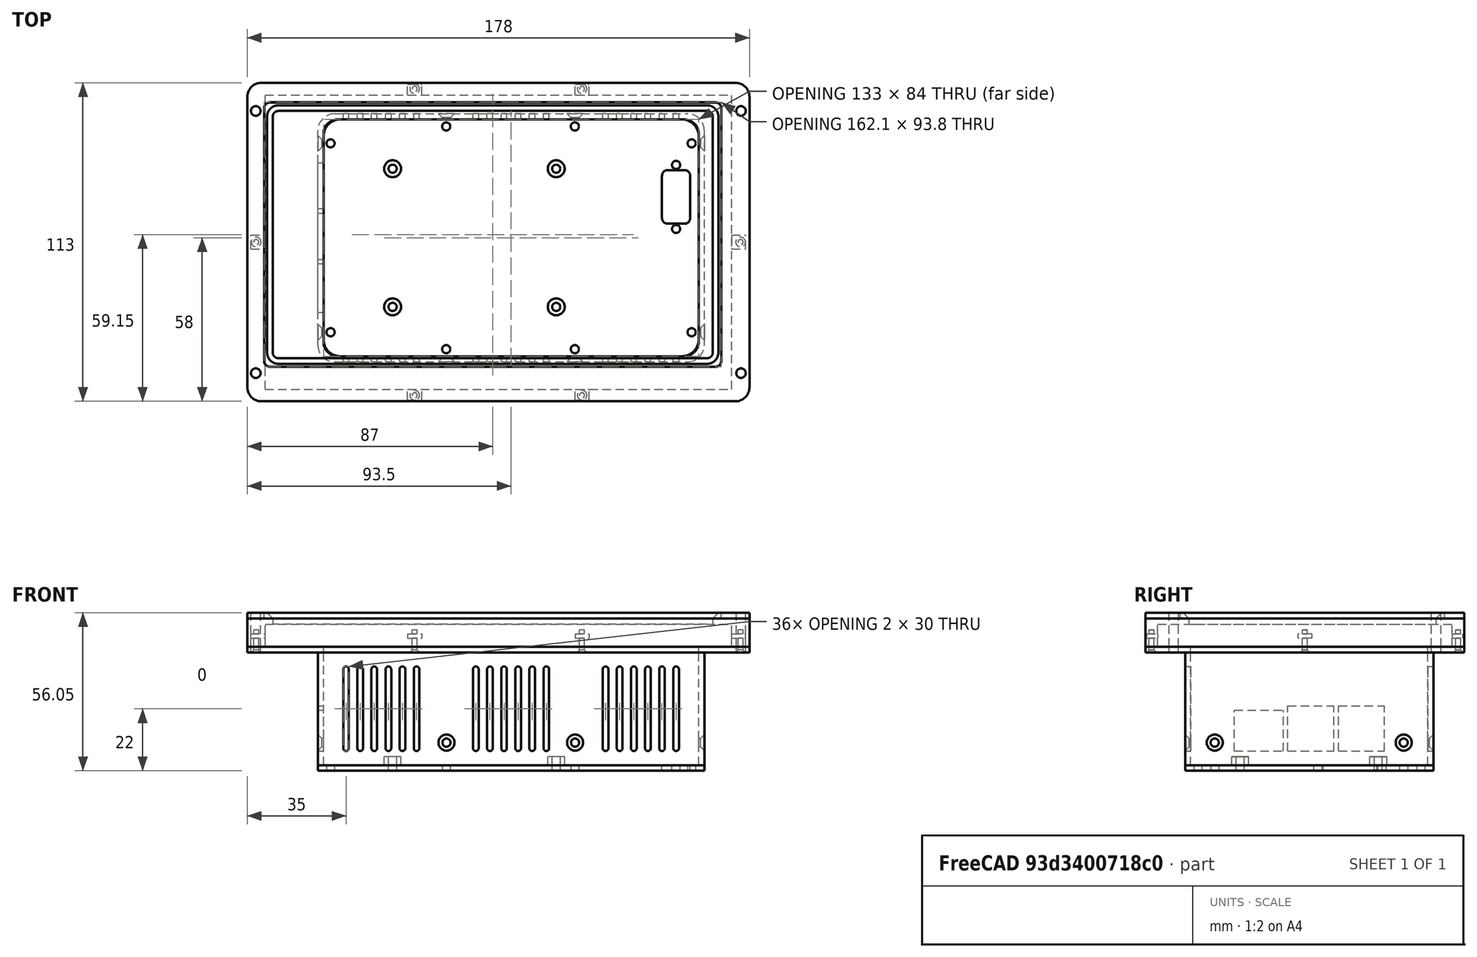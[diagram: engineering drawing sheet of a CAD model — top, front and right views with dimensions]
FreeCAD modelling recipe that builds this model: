
FCSTD DOCUMENT  (FreeCAD 0.20R29603 (Git))
Label: RPI4Soar_V2
License: All rights reserved
LicenseURL: http://en.wikipedia.org/wiki/All_rights_reserved
objects: Part::Cut×76, Part::Box×42, Part::Cylinder×28, Part::Fillet×17, Part::Fuse×5, Part::FeaturePython×4, Part::Chamfer×3, Spreadsheet::Sheet×1
note: 175 computed .brp shape members not serialized (recipe doc carries the construction recipe); baked Part::Feature solids carry a one-line shape summary decoded from their .brp

FEATURE [Spreadsheet::Sheet] Spreadsheet
  cells = A1=Display Abmessungen; C1=Toleranz; A2=Länge / mm; B2=165; C2=0.4; D2==B2 + C2; A3=Breite / mm; B3=104; C3=0.4; D3==B3 + C3; A4=Höhe / mm; B4=7.05; C4=1; D4==B4 + C4; A6=Gehäuse Dimensionen; A7=Länge / mm; B7=178; A8=Breite /mm; B8=113; A9=Höhe / mm; B9=30
FEATURE [Part::Box] Box  label="Würfel"
  AttacherType = Attacher::AttachEngine3D
  Height = 10.05
  Length = 178
  Width = 113
  expr: Height = Spreadsheet.D4 + 2
  expr: Length = Spreadsheet.B7
  expr: Width = Spreadsheet.B8
FEATURE [Part::Box] Box001  label="Würfel001"
  AttacherType = Attacher::AttachEngine3D
  Height = 8.05
  Length = 165.4
  Placement = pos=(6.3,4.3,0) rot=(0,0,1;0rad)
  Width = 104.4
  expr: .Placement.Base.x = (Spreadsheet.B7 - Spreadsheet.D2) / 2
  expr: .Placement.Base.y = (Spreadsheet.B8 - Spreadsheet.D3) / 2
  expr: Height = Spreadsheet.D4
  expr: Length = Spreadsheet.D2
  expr: Width = Spreadsheet.D3
FEATURE [Part::Cylinder] Cylinder  label="Zylinder"
  Angle = 360
  AttacherType = Attacher::AttachEngine3D
  FirstAngle = 0
  Height = 17
  Placement = pos=(3,10,-5) rot=(0,0,1;0rad)
  Radius = 1.7
  SecondAngle = 0
  expr: .Placement.Base.x = (Spreadsheet.B7 - 172) / 2
  expr: .Placement.Base.y = (Spreadsheet.B8 - 93) / 2
FEATURE [Part::Cylinder] Cylinder001  label="Zylinder001"
  Angle = 360
  AttacherType = Attacher::AttachEngine3D
  FirstAngle = 0
  Height = 17
  Placement = pos=(3,103,-5) rot=(0,0,1;0rad)
  Radius = 1.7
  SecondAngle = 0
  expr: .Placement.Base.x = (Spreadsheet.B7 - 172) / 2
  expr: .Placement.Base.y = Spreadsheet.B8 - (Spreadsheet.B8 - 93) / 2
FEATURE [Part::Cylinder] Cylinder002  label="Zylinder002"
  Angle = 360
  AttacherType = Attacher::AttachEngine3D
  FirstAngle = 0
  Height = 17
  Placement = pos=(175,10,-5) rot=(0,0,1;0rad)
  Radius = 1.7
  SecondAngle = 0
  expr: .Placement.Base.x = Spreadsheet.B7 - (Spreadsheet.B7 - 172) / 2
  expr: .Placement.Base.y = (Spreadsheet.B8 - 93) / 2
FEATURE [Part::Cylinder] Cylinder003  label="Zylinder003"
  Angle = 360
  AttacherType = Attacher::AttachEngine3D
  FirstAngle = 0
  Height = 17
  Placement = pos=(175,103,-5) rot=(0,0,1;0rad)
  Radius = 1.7
  SecondAngle = 0
  expr: .Placement.Base.x = Spreadsheet.B7 - (Spreadsheet.B7 - 172) / 2
  expr: .Placement.Base.y = Spreadsheet.B8 - (Spreadsheet.B8 - 93) / 2
FEATURE [Part::Box] Box004  label="Würfel004"
  AttacherType = Attacher::AttachEngine3D
  Height = 2
  Length = 178
  Placement = pos=(0,0,-2) rot=(0,0,1;0rad)
  Width = 113
  expr: Length = Spreadsheet.B7
  expr: Width = Spreadsheet.B8
FEATURE [Part::Box] Box005  label="Würfel005"
  AttacherType = Attacher::AttachEngine3D
  Height = 15
  Length = 133
  Placement = pos=(27,16,-14) rot=(0,0,1;0rad)
  Width = 84
FEATURE [Part::Box] Box006  label="Würfel006"
  AttacherType = Attacher::AttachEngine3D
  Height = 7.05
  Length = 156
  Placement = pos=(9,15.3,3) rot=(0,0,1;0rad)
  Width = 87.7
  expr: .Placement.Base.x = 15.5 - 6.5
  expr: .Placement.Base.y = 20.8 - 5.5
  expr: Height = Spreadsheet.B4
FEATURE [Part::Fillet] Fillet003
  Base = -> Box005
  Edges = 4 edges r=5: [Edge1,Edge3,Edge5,Edge7]
FEATURE [Part::Cut] Cut011
  Base = -> Box004
  Tool = -> Fillet003
FEATURE [Part::Cut] Cut012
  Base = -> Cut011
  Tool = -> Cylinder001
FEATURE [Part::Cut] Cut013
  Base = -> Cut012
  Tool = -> Cylinder002
FEATURE [Part::Cut] Cut014
  Base = -> Cut013
  Tool = -> Cylinder003
FEATURE [Part::Cut] Cut015
  Base = -> Cut014
  Tool = -> Cylinder
FEATURE [Part::Fillet] Fillet004
  Base = -> Cut015
  Edges = 4 edges r=5: [Edge1,Edge3,Edge6,Edge23]
FEATURE [Part::Box] Box007  label="Würfel007"
  AttacherType = Attacher::AttachEngine3D
  Height = 40
  Length = 133
  Placement = pos=(27,16,-42) rot=(0,0,1;0rad)
  Width = 84
FEATURE [Part::Box] Box008  label="Würfel008"
  AttacherType = Attacher::AttachEngine3D
  Height = 40
  Length = 137
  Placement = pos=(25,14,-42) rot=(0,0,1;0rad)
  Width = 88
FEATURE [Part::Box] Box010  label="Würfel010"
  AttacherType = Attacher::AttachEngine3D
  Height = 2
  Length = 137
  Placement = pos=(25,14,-44) rot=(0,0,1;0rad)
  Width = 88
FEATURE [Part::Cylinder] Cylinder008  label="Zylinder008"
  Angle = 360
  AttacherType = Attacher::AttachEngine3D
  FirstAngle = 0
  Height = 108
  Placement = pos=(116.2,114,-34) rot=(1,0,0;1.5708rad)
  Radius = 1.45
  SecondAngle = 0
FEATURE [Part::Cylinder] Cylinder010  label="Zylinder010"
  Angle = 360
  AttacherType = Attacher::AttachEngine3D
  FirstAngle = 0
  Height = 155
  Placement = pos=(14,24.5,-34) rot=(0,1,0;1.5708rad)
  Radius = 1.45
  SecondAngle = 0
FEATURE [Part::Cylinder] Cylinder011  label="Zylinder011"
  Angle = 360
  AttacherType = Attacher::AttachEngine3D
  FirstAngle = 0
  Height = 157
  Placement = pos=(14,91.5,-34) rot=(0,1,0;1.5708rad)
  Radius = 1.45
  SecondAngle = 0
FEATURE [Part::Cylinder] Cylinder012  label="Zylinder012"
  Angle = 360
  AttacherType = Attacher::AttachEngine3D
  FirstAngle = 0
  Height = 10
  Placement = pos=(109.5,33.5,-49) rot=(0,0,1;0rad)
  Radius = 1.45
  SecondAngle = 0
  expr: .Placement.Base.y = 35 - 1.5
FEATURE [Part::Cylinder] Cylinder013  label="Zylinder013"
  Angle = 360
  AttacherType = Attacher::AttachEngine3D
  FirstAngle = 0
  Height = 10
  Placement = pos=(51.5,82.5,-49) rot=(0,0,1;0rad)
  Radius = 1.45
  SecondAngle = 0
  expr: .Placement.Base.y = 35 + 49 - 1.5
FEATURE [Part::Cylinder] Cylinder014  label="Zylinder014"
  Angle = 360
  AttacherType = Attacher::AttachEngine3D
  FirstAngle = 0
  Height = 10
  Placement = pos=(51.5,33.5,-49) rot=(0,0,1;0rad)
  Radius = 1.45
  SecondAngle = 0
  expr: .Placement.Base.y = 35 - 1.5
FEATURE [Part::Cylinder] Cylinder015  label="Zylinder015"
  Angle = 360
  AttacherType = Attacher::AttachEngine3D
  FirstAngle = 0
  Height = 10
  Placement = pos=(109.5,82.5,-49) rot=(0,0,1;0rad)
  Radius = 1.45
  SecondAngle = 0
  expr: .Placement.Base.y = 35 + 49 - 1.5
FEATURE [Part::Box] Box017  label="Würfel017"
  AttacherType = Attacher::AttachEngine3D
  Height = 10
  Length = 10
  Placement = pos=(147,63,-49) rot=(0,0,1;0rad)
  Width = 19
FEATURE [Part::Cylinder] Cylinder020  label="Zylinder020"
  Angle = 360
  AttacherType = Attacher::AttachEngine3D
  FirstAngle = 0
  Height = 10
  Placement = pos=(152,83.85,-49) rot=(0,0,1;0rad)
  Radius = 1.45
  SecondAngle = 0
FEATURE [Part::Cylinder] Cylinder021  label="Zylinder021"
  Angle = 360
  AttacherType = Attacher::AttachEngine3D
  FirstAngle = 0
  Height = 10
  Placement = pos=(152,61.15,-49) rot=(0,0,1;0rad)
  Radius = 1.45
  SecondAngle = 0
FEATURE [Part::Cylinder] Cylinder022  label="Zylinder022"
  Angle = 360
  AttacherType = Attacher::AttachEngine3D
  FirstAngle = 0
  Height = 10
  Placement = pos=(59.3333,2.15,-4) rot=(0,0,1;0rad)
  Radius = 0.9
  SecondAngle = 0
  expr: .Placement.Base.x = Spreadsheet.B7 / 3
  expr: .Placement.Base.y = (Spreadsheet.B8 - Spreadsheet.D3) / 4
FEATURE [Part::Cylinder] Cylinder023  label="Zylinder023"
  Angle = 360
  AttacherType = Attacher::AttachEngine3D
  FirstAngle = 0
  Height = 10
  Placement = pos=(118.667,2.15,-4) rot=(0,0,1;0rad)
  Radius = 0.9
  SecondAngle = 0
  expr: .Placement.Base.x = Spreadsheet.B7 / 3 * 2
  expr: .Placement.Base.y = (Spreadsheet.B8 - Spreadsheet.D3) / 4
FEATURE [Part::Box] Box018  label="Würfel018"
  AttacherType = Attacher::AttachEngine3D
  Height = 1.5
  Length = 5
  Placement = pos=(56.8333,0.5,3) rot=(0,0,1;0rad)
  Width = 4
  expr: .Placement.Base.x = Spreadsheet.B7 / 3 - 2.5
FEATURE [Part::Box] Box019  label="Würfel019"
  AttacherType = Attacher::AttachEngine3D
  Height = 1.5
  Length = 5
  Placement = pos=(116.167,0.5,3) rot=(0,0,1;0rad)
  Width = 4
  expr: .Placement.Base.x = Spreadsheet.B7 / 3 * 2 - 2.5
FEATURE [Part::Cylinder] Cylinder024  label="Zylinder024"
  Angle = 360
  AttacherType = Attacher::AttachEngine3D
  FirstAngle = 0
  Height = 10
  Placement = pos=(59.3333,110.85,-4) rot=(0,0,1;0rad)
  Radius = 0.9
  SecondAngle = 0
  expr: .Placement.Base.x = Spreadsheet.B7 / 3
  expr: .Placement.Base.y = Spreadsheet.B8 - (Spreadsheet.B8 - Spreadsheet.D3) / 4
FEATURE [Part::Cylinder] Cylinder025  label="Zylinder025"
  Angle = 360
  AttacherType = Attacher::AttachEngine3D
  FirstAngle = 0
  Height = 10
  Placement = pos=(118.667,110.85,-4) rot=(0,0,1;0rad)
  Radius = 0.9
  SecondAngle = 0
  expr: .Placement.Base.x = Spreadsheet.B7 / 3 * 2
  expr: .Placement.Base.y = Spreadsheet.B8 - (Spreadsheet.B8 - Spreadsheet.D3) / 4
FEATURE [Part::Box] Box020  label="Würfel020"
  AttacherType = Attacher::AttachEngine3D
  Height = 1.5
  Length = 5
  Placement = pos=(56.8333,108.5,3) rot=(0,0,1;0rad)
  Width = 4
  expr: .Placement.Base.x = Spreadsheet.B7 / 3 - 2.5
FEATURE [Part::Cylinder] Cylinder026  label="Zylinder026"
  Angle = 360
  AttacherType = Attacher::AttachEngine3D
  FirstAngle = 0
  Height = 10
  Placement = pos=(3.15,56.5,-4) rot=(0,0,1;0rad)
  Radius = 0.9
  SecondAngle = 0
  expr: .Placement.Base.x = (Spreadsheet.B7 - Spreadsheet.D2) / 4
  expr: .Placement.Base.y = Spreadsheet.B8 / 2
FEATURE [Part::Cylinder] Cylinder027  label="Zylinder027"
  Angle = 360
  AttacherType = Attacher::AttachEngine3D
  FirstAngle = 0
  Height = 10
  Placement = pos=(174.85,56.5,-4) rot=(0,0,1;0rad)
  Radius = 0.9
  SecondAngle = 0
  expr: .Placement.Base.x = Spreadsheet.B7 - (Spreadsheet.B7 - Spreadsheet.D2) / 4
  expr: .Placement.Base.y = Spreadsheet.B8 / 2
FEATURE [Part::Box] Box021  label="Würfel021"
  AttacherType = Attacher::AttachEngine3D
  Height = 1.5
  Length = 6
  Placement = pos=(1.3,54,3) rot=(0,0,1;0rad)
  Width = 5
  expr: .Placement.Base.y = Spreadsheet.B8 / 2 - 2.5
FEATURE [Part::Box] Box022  label="Würfel022"
  AttacherType = Attacher::AttachEngine3D
  Height = 1.5
  Length = 6
  Placement = pos=(170.7,54,3) rot=(0,0,1;0rad)
  Width = 5
  expr: .Placement.Base.y = Spreadsheet.B8 / 2 - 2.5
FEATURE [Part::Cut] Cut
  Base = -> Box
  Tool = -> Box001
FEATURE [Part::Cut] Cut038
  Base = -> Cut
  Tool = -> Box006
FEATURE [Part::Fillet] Fillet
  Base = -> Cut038
  Edges = 4 edges r=5: [Edge1,Edge3,Edge6,Edge15]
FEATURE [Part::Cut] Cut054
  Base = -> Box008
  Tool = -> Box007
FEATURE [Part::Cut] Cut060
  Base = -> Fillet004
  Tool = -> Cylinder022
FEATURE [Part::Cut] Cut061
  Base = -> Cut060
  Tool = -> Cylinder022
FEATURE [Part::Cut] Cut062
  Base = -> Cut061
  Tool = -> Cylinder024
FEATURE [Part::Cut] Cut063
  Base = -> Cut062
  Tool = -> Cylinder025
FEATURE [Part::Cut] Cut064
  Base = -> Cut063
  Tool = -> Cylinder026
FEATURE [Part::Cut] Cut065
  Base = -> Cut064
  Tool = -> Cylinder027
FEATURE [Part::Cut] Cut066
  Base = -> Cut065
  Tool = -> Cylinder023
FEATURE [Part::Box] Box023  label="Würfel023"
  AttacherType = Attacher::AttachEngine3D
  Height = 1.5
  Length = 5
  Placement = pos=(116.167,108.5,3) rot=(0,0,1;0rad)
  Width = 4
  expr: .Placement.Base.x = Spreadsheet.B7 / 3 * 2 - 2.5
FEATURE [Part::Cylinder] Cylinder032  label="Zylinder032"
  Angle = 360
  AttacherType = Attacher::AttachEngine3D
  FirstAngle = 0
  Height = 108
  Placement = pos=(70.6,114,-34) rot=(1,0,0;1.5708rad)
  Radius = 1.45
  SecondAngle = 0
FEATURE [Part::Cylinder] Cylinder033  label="Zylinder033"
  Angle = 360
  AttacherType = Attacher::AttachEngine3D
  FirstAngle = 0
  Height = 10
  Placement = pos=(116.1,97.5,-49) rot=(0,0,1;0rad)
  Radius = 1.45
  SecondAngle = 0
FEATURE [Part::Cylinder] Cylinder034  label="Zylinder034"
  Angle = 360
  AttacherType = Attacher::AttachEngine3D
  FirstAngle = 0
  Height = 10
  Placement = pos=(116.1,18.5,-49) rot=(0,0,1;0rad)
  Radius = 1.45
  SecondAngle = 0
FEATURE [Part::Cylinder] Cylinder035  label="Zylinder035"
  Angle = 360
  AttacherType = Attacher::AttachEngine3D
  FirstAngle = 0
  Height = 10
  Placement = pos=(70.5,97.5,-49) rot=(0,0,1;0rad)
  Radius = 1.45
  SecondAngle = 0
FEATURE [Part::Cylinder] Cylinder036  label="Zylinder036"
  Angle = 360
  AttacherType = Attacher::AttachEngine3D
  FirstAngle = 0
  Height = 10
  Placement = pos=(70.5,18.5,-49) rot=(0,0,1;0rad)
  Radius = 1.45
  SecondAngle = 0
FEATURE [Part::Cylinder] Cylinder037  label="Zylinder037"
  Angle = 360
  AttacherType = Attacher::AttachEngine3D
  FirstAngle = 0
  Height = 10
  Placement = pos=(29.5,91.5,-49) rot=(0,0,1;0rad)
  Radius = 1.45
  SecondAngle = 0
FEATURE [Part::Cylinder] Cylinder038  label="Zylinder038"
  Angle = 360
  AttacherType = Attacher::AttachEngine3D
  FirstAngle = 0
  Height = 10
  Placement = pos=(157.5,91.5,-49) rot=(0,0,1;0rad)
  Radius = 1.45
  SecondAngle = 0
FEATURE [Part::Cylinder] Cylinder039  label="Zylinder039"
  Angle = 360
  AttacherType = Attacher::AttachEngine3D
  FirstAngle = 0
  Height = 10
  Placement = pos=(157.5,24.5,-49) rot=(0,0,1;0rad)
  Radius = 1.45
  SecondAngle = 0
FEATURE [Part::Cylinder] Cylinder040  label="Zylinder040"
  Angle = 360
  AttacherType = Attacher::AttachEngine3D
  FirstAngle = 0
  Height = 10
  Placement = pos=(29.5,24.5,-49) rot=(0,0,1;0rad)
  Radius = 1.45
  SecondAngle = 0
FEATURE [Part::Cut] Cut089
  Base = -> Cut054
  Tool = -> Cylinder008
FEATURE [Part::Cut] Cut090
  Base = -> Cut089
  Tool = -> Cylinder010
FEATURE [Part::Cut] Cut091
  Base = -> Cut090
  Tool = -> Cylinder011
FEATURE [Part::Cut] Cut092
  Base = -> Cut091
  Tool = -> Cylinder032
FEATURE [Part::Fillet] Fillet013
  Base = -> Cut092
  Edges = 8 edges r=6: [Edge1,Edge4,Edge8,Edge24,Edge37,Edge38,Edge39,Edge40]
FEATURE [Part::Fillet] Fillet014
  Base = -> Box010
  Edges = 4 edges r=6: [Edge1,Edge3,Edge5,Edge7]
FEATURE [Part::Cut] Cut093
  Base = -> Fillet014
  Tool = -> Cylinder033
FEATURE [Part::Cut] Cut094
  Base = -> Cut093
  Tool = -> Cylinder034
FEATURE [Part::Cut] Cut095
  Base = -> Cut094
  Tool = -> Cylinder035
FEATURE [Part::Cut] Cut096
  Base = -> Cut095
  Tool = -> Cylinder036
FEATURE [Part::Cut] Cut097
  Base = -> Cut096
  Tool = -> Cylinder037
FEATURE [Part::Cut] Cut098
  Base = -> Cut097
  Tool = -> Cylinder038
FEATURE [Part::Cut] Cut099
  Base = -> Cut098
  Tool = -> Cylinder039
FEATURE [Part::Cut] Cut100
  Base = -> Cut099
  Tool = -> Cylinder040
FEATURE [Part::Cut] Cut101
  Base = -> Cut100
  Tool = -> Cylinder012
FEATURE [Part::Cut] Cut102
  Base = -> Cut101
  Tool = -> Cylinder013
FEATURE [Part::Cut] Cut103
  Base = -> Cut102
  Tool = -> Cylinder014
FEATURE [Part::Cut] Cut104
  Base = -> Cut103
  Tool = -> Cylinder015
FEATURE [Part::FeaturePython] Tube  label="Spacer"  # WARN: FeaturePython — macro-defined, semantics opaque (R4)
  AttacherType = Attacher::AttachEngine3D
  Height = 3
  InnerRadius = 1.45
  OuterRadius = 3
  Placement = pos=(109.5,33.5,-42) rot=(0,0,1;0rad)
FEATURE [Part::Chamfer] Chamfer005
  Base = -> Fillet013
  Edges = 8 edges r=1.4: [Edge5,Edge6,Edge44,Edge45,Edge47,Edge48,Edge51,Edge52]
FEATURE [Part::Fuse] Fusion021
  Base = -> Chamfer005
  Tool = -> Cut066
FEATURE [Part::Chamfer] Chamfer006
  Base = -> Fusion021
  Edges = 6 edges r=0.8: [Edge18,Edge19,Edge21,Edge23,Edge31,Edge32]
FEATURE [Part::Box] Box034  label="Würfel034"
  AttacherType = Attacher::AttachEngine3D
  Height = 14.5
  Length = 2
  Placement = pos=(25,31.5,-37) rot=(0,0,1;0rad)
  Width = 17.3
FEATURE [Part::Box] Box035  label="Würfel035"
  AttacherType = Attacher::AttachEngine3D
  Height = 16
  Length = 2
  Placement = pos=(25,50.4,-37) rot=(0,0,1;0rad)
  Width = 16.3
FEATURE [Part::Box] Box036  label="Würfel036"
  AttacherType = Attacher::AttachEngine3D
  Height = 16
  Length = 2
  Placement = pos=(25,68.4,-37) rot=(0,0,1;0rad)
  Width = 16.3
FEATURE [Part::Cut] Cut105
  Base = -> Chamfer006
  Tool = -> Box034
FEATURE [Part::Cut] Cut106
  Base = -> Cut105
  Tool = -> Box035
FEATURE [Part::Cut] Cut107  label="Housing_1"
  Base = -> Cut106
  Tool = -> Box036
FEATURE [Part::Fillet] Fillet015
  Base = -> Box017
  Edges = 4 edges r=2: [Edge1,Edge3,Edge5,Edge7]
FEATURE [Part::Cut] Cut108
  Base = -> Cut104
  Tool = -> Fillet015
FEATURE [Part::Cut] Cut109
  Base = -> Cut108
  Tool = -> Cylinder020
FEATURE [Part::Cut] Cut110  label="Backplate"
  Base = -> Cut109
  Tool = -> Cylinder021
FEATURE [Part::FeaturePython] Tube001  label="Spacer1"  # WARN: FeaturePython — macro-defined, semantics opaque (R4)
  AttacherType = Attacher::AttachEngine3D
  Height = 3
  InnerRadius = 1.45
  OuterRadius = 3
  Placement = pos=(51.5,33.5,-42) rot=(0,0,1;0rad)
FEATURE [Part::FeaturePython] Tube002  label="Spacer2"  # WARN: FeaturePython — macro-defined, semantics opaque (R4)
  AttacherType = Attacher::AttachEngine3D
  Height = 3
  InnerRadius = 1.45
  OuterRadius = 3
  Placement = pos=(109.5,82.5,-42) rot=(0,0,1;0rad)
FEATURE [Part::FeaturePython] Tube003  label="Spacer3"  # WARN: FeaturePython — macro-defined, semantics opaque (R4)
  AttacherType = Attacher::AttachEngine3D
  Height = 3
  InnerRadius = 1.45
  OuterRadius = 3
  Placement = pos=(51.5,82.5,-42) rot=(0,0,1;0rad)
FEATURE [Part::Box] Box037  label="Würfel037"
  AttacherType = Attacher::AttachEngine3D
  Height = 30
  Length = 2
  Placement = pos=(34,0,-37) rot=(0,0,1;0rad)
  Width = 113
FEATURE [Part::Box] Box038  label="Würfel038"
  AttacherType = Attacher::AttachEngine3D
  Height = 30
  Length = 2
  Placement = pos=(39,0,-37) rot=(0,0,1;0rad)
  Width = 113
FEATURE [Part::Box] Box039  label="Würfel039"
  AttacherType = Attacher::AttachEngine3D
  Height = 30
  Length = 2
  Placement = pos=(44,0,-37) rot=(0,0,1;0rad)
  Width = 113
FEATURE [Part::Box] Box040  label="Würfel040"
  AttacherType = Attacher::AttachEngine3D
  Height = 30
  Length = 2
  Placement = pos=(49,0,-37) rot=(0,0,1;0rad)
  Width = 113
FEATURE [Part::Box] Box041  label="Würfel041"
  AttacherType = Attacher::AttachEngine3D
  Height = 30
  Length = 2
  Placement = pos=(54,0,-37) rot=(0,0,1;0rad)
  Width = 113
FEATURE [Part::Box] Box042  label="Würfel042"
  AttacherType = Attacher::AttachEngine3D
  Height = 30
  Length = 2
  Placement = pos=(59,0,-37) rot=(0,0,1;0rad)
  Width = 113
FEATURE [Part::Box] Box043  label="Würfel043"
  AttacherType = Attacher::AttachEngine3D
  Height = 30
  Length = 2
  Placement = pos=(80,0,-37) rot=(0,0,1;0rad)
  Width = 113
FEATURE [Part::Box] Box044  label="Würfel044"
  AttacherType = Attacher::AttachEngine3D
  Height = 30
  Length = 2
  Placement = pos=(85,0,-37) rot=(0,0,1;0rad)
  Width = 113
FEATURE [Part::Box] Box045  label="Würfel045"
  AttacherType = Attacher::AttachEngine3D
  Height = 30
  Length = 2
  Placement = pos=(90,0,-37) rot=(0,0,1;0rad)
  Width = 113
FEATURE [Part::Box] Box046  label="Würfel046"
  AttacherType = Attacher::AttachEngine3D
  Height = 30
  Length = 2
  Placement = pos=(95,0,-37) rot=(0,0,1;0rad)
  Width = 113
FEATURE [Part::Box] Box047  label="Würfel047"
  AttacherType = Attacher::AttachEngine3D
  Height = 30
  Length = 2
  Placement = pos=(100,0,-37) rot=(0,0,1;0rad)
  Width = 113
FEATURE [Part::Box] Box048  label="Würfel048"
  AttacherType = Attacher::AttachEngine3D
  Height = 30
  Length = 2
  Placement = pos=(105,0,-37) rot=(0,0,1;0rad)
  Width = 113
FEATURE [Part::Box] Box049  label="Würfel049"
  AttacherType = Attacher::AttachEngine3D
  Height = 30
  Length = 2
  Placement = pos=(126,0,-37) rot=(0,0,1;0rad)
  Width = 113
FEATURE [Part::Box] Box050  label="Würfel050"
  AttacherType = Attacher::AttachEngine3D
  Height = 30
  Length = 2
  Placement = pos=(131,0,-37) rot=(0,0,1;0rad)
  Width = 113
FEATURE [Part::Box] Box051  label="Würfel051"
  AttacherType = Attacher::AttachEngine3D
  Height = 30
  Length = 2
  Placement = pos=(136,0,-37) rot=(0,0,1;0rad)
  Width = 113
FEATURE [Part::Box] Box052  label="Würfel052"
  AttacherType = Attacher::AttachEngine3D
  Height = 30
  Length = 2
  Placement = pos=(141,0,-37) rot=(0,0,1;0rad)
  Width = 113
FEATURE [Part::Box] Box053  label="Würfel053"
  AttacherType = Attacher::AttachEngine3D
  Height = 30
  Length = 2
  Placement = pos=(146,0,-37) rot=(0,0,1;0rad)
  Width = 113
FEATURE [Part::Box] Box054  label="Würfel054"
  AttacherType = Attacher::AttachEngine3D
  Height = 30
  Length = 2
  Placement = pos=(151,0,-37) rot=(0,0,1;0rad)
  Width = 113
FEATURE [Part::Cut] Cut111
  Base = -> Cut107
  Tool = -> Box037
FEATURE [Part::Cut] Cut112
  Base = -> Cut111
  Tool = -> Box038
FEATURE [Part::Cut] Cut113
  Base = -> Cut112
  Tool = -> Box039
FEATURE [Part::Cut] Cut114
  Base = -> Cut113
  Tool = -> Box040
FEATURE [Part::Cut] Cut115
  Base = -> Cut114
  Tool = -> Box041
FEATURE [Part::Cut] Cut116
  Base = -> Cut115
  Tool = -> Box042
FEATURE [Part::Cut] Cut117
  Base = -> Cut116
  Tool = -> Box043
FEATURE [Part::Cut] Cut118
  Base = -> Cut117
  Tool = -> Box044
FEATURE [Part::Cut] Cut119
  Base = -> Cut118
  Tool = -> Box045
FEATURE [Part::Cut] Cut120
  Base = -> Cut119
  Tool = -> Box046
FEATURE [Part::Cut] Cut121
  Base = -> Cut120
  Tool = -> Box047
FEATURE [Part::Cut] Cut122
  Base = -> Cut121
  Tool = -> Box048
FEATURE [Part::Cut] Cut123
  Base = -> Cut122
  Tool = -> Box049
FEATURE [Part::Cut] Cut124
  Base = -> Cut123
  Tool = -> Box050
FEATURE [Part::Cut] Cut125
  Base = -> Cut124
  Tool = -> Box051
FEATURE [Part::Cut] Cut126
  Base = -> Cut125
  Tool = -> Box052
FEATURE [Part::Cut] Cut127
  Base = -> Cut126
  Tool = -> Box053
FEATURE [Part::Cut] Cut128  label="housing2"
  Base = -> Cut127
  Tool = -> Box054
FEATURE [Part::Box] Box055  label="Würfel055"
  AttacherType = Attacher::AttachEngine3D
  Height = 2
  Length = 162
  Placement = pos=(6,12.3,10.05) rot=(0,0,1;0rad)
  Width = 3
FEATURE [Part::Box] Box056  label="Würfel056"
  AttacherType = Attacher::AttachEngine3D
  Height = 2
  Length = 162
  Placement = pos=(6,103,10.05) rot=(0,0,1;0rad)
  Width = 3
FEATURE [Part::Box] Box057  label="Würfel057"
  AttacherType = Attacher::AttachEngine3D
  Height = 2
  Length = 3
  Placement = pos=(6,12.3,10.05) rot=(0,0,1;0rad)
  Width = 93.7
FEATURE [Part::Box] Box058  label="Würfel058"
  AttacherType = Attacher::AttachEngine3D
  Height = 2
  Length = 3
  Placement = pos=(165,12.3,10.05) rot=(0,0,1;0rad)
  Width = 93.7
FEATURE [Part::Cut] Cut129
  Base = -> Fillet
  Tool = -> Box018
FEATURE [Part::Cut] Cut130
  Base = -> Cut129
  Tool = -> Box019
FEATURE [Part::Cut] Cut131
  Base = -> Cut130
  Tool = -> Box020
FEATURE [Part::Cut] Cut132
  Base = -> Cut131
  Tool = -> Box021
FEATURE [Part::Cut] Cut133
  Base = -> Cut132
  Tool = -> Box022
FEATURE [Part::Cut] Cut134
  Base = -> Cut133
  Tool = -> Box023
FEATURE [Part::Cut] Cut135
  Base = -> Cut134
  Tool = -> Cylinder023
FEATURE [Part::Cut] Cut136
  Base = -> Cut135
  Tool = -> Cylinder024
FEATURE [Part::Cut] Cut137
  Base = -> Cut136
  Tool = -> Cylinder025
FEATURE [Part::Cut] Cut138
  Base = -> Cut137
  Tool = -> Cylinder026
FEATURE [Part::Cut] Cut139
  Base = -> Cut138
  Tool = -> Cylinder027
FEATURE [Part::Cut] Cut140
  Base = -> Cut139
  Tool = -> Cylinder022
FEATURE [Part::Cut] Cut141
  Base = -> Cut140
  Tool = -> Cylinder
FEATURE [Part::Cut] Cut142
  Base = -> Cut141
  Tool = -> Cylinder001
FEATURE [Part::Cut] Cut143
  Base = -> Cut142
  Tool = -> Cylinder002
FEATURE [Part::Cut] Cut144
  Base = -> Cut143
  Tool = -> Cylinder003
FEATURE [Part::Fillet] Fillet017
  Base = -> Cut128
  Edges = 24 edges r=0.99: [Edge296,Edge297,Edge299,Edge301,Edge304,Edge305,Edge307,Edge309,Edge312,Edge313,Edge315,Edge317,Edge320,Edge321,Edge323,Edge325,Edge328,Edge329,Edge331,Edge333,Edge336,Edge337,Edge339,Edge341]
FEATURE [Part::Fillet] Fillet018
  Base = -> Fillet017
  Edges = 23 edges r=0.99: [Edge163,Edge164,Edge166,Edge168,Edge171,Edge172,Edge174,Edge176,Edge179,Edge180,Edge182,Edge184,Edge189,Edge190,Edge192,Edge194,Edge197,Edge198,Edge200,Edge202,Edge206,Edge208,Edge210]
FEATURE [Part::Fillet] Fillet019
  Base = -> Fillet018
  Edges = 1 edges r=0.99: [Edge396]
FEATURE [Part::Fillet] Fillet020
  Base = -> Fillet019
  Edges = 24 edges r=0.99: [Edge221,Edge222,Edge224,Edge226,Edge229,Edge230,Edge232,Edge234,Edge237,Edge238,Edge240,Edge242,Edge245,Edge246,Edge248,Edge250,Edge253,Edge254,Edge256,Edge258,Edge261,Edge262,Edge264,Edge266]
FEATURE [Part::Fillet] Fillet021
  Base = -> Fillet020
  Edges = 23 edges r=0.99: [Edge798,Edge799,Edge801,Edge802,Edge803,Edge804,Edge805,Edge806,Edge807,Edge808,Edge809,Edge810,Edge811,Edge812,Edge813,Edge814,Edge815,Edge816,Edge817,Edge818,Edge819,Edge820,Edge821]
FEATURE [Part::Fillet] Fillet022
  Base = -> Fillet021
  Edges = 1 edges r=0.99: [Edge110]
FEATURE [Part::Fillet] Fillet023
  Base = -> Fillet022
  Edges = 24 edges r=0.99: [Edge211,Edge213,Edge215,Edge217,Edge219,Edge221,Edge223,Edge225,Edge227,Edge229,Edge231,Edge233,Edge237,Edge239,Edge241,Edge243,Edge245,Edge247,Edge249,Edge251,Edge253,Edge255,Edge257,Edge259]
FEATURE [Part::Fillet] Fillet024  label="housing"
  Base = -> Fillet023
  Edges = 24 edges r=0.99: [Edge203,Edge205,Edge207,Edge209,Edge211,Edge213,Edge215,Edge217,Edge219,Edge221,Edge223,Edge225,Edge227,Edge229,Edge231,Edge233,Edge235,Edge237,Edge239,Edge241,Edge243,Edge245,Edge247,Edge249]
FEATURE [Part::Fuse] Fusion
  Base = -> Cut144
  Tool = -> Box055
FEATURE [Part::Fuse] Fusion022
  Base = -> Fusion
  Tool = -> Box056
FEATURE [Part::Fuse] Fusion023
  Base = -> Fusion022
  Tool = -> Box057
FEATURE [Part::Fuse] Fusion024
  Base = -> Fusion023
  Tool = -> Box058
FEATURE [Part::Fillet] Fillet025
  Base = -> Fusion024
  Edges = 8 edges r=2: [Edge2,Edge54,Edge61,Edge67,Edge95,Edge96,Edge98,Edge144]
FEATURE [Part::Chamfer] Chamfer  label="frame"
  Base = -> Fillet025
  Edges = 1 edges r=1.99: [Edge96]
FEATURE [Part::Box] Box059  label="Würfel059"
  AttacherType = Attacher::AttachEngine3D
  Height = 2
  Length = 178
  Placement = pos=(0,0,10) rot=(0,0,1;0rad)
  Width = 113
FEATURE [Part::Fillet] Fillet026
  Base = -> Box059
  Edges = 4 edges r=5: [Edge1,Edge3,Edge5,Edge7]
FEATURE [Part::Cut] Cut145
  Base = -> Fillet026
  Tool = -> Cylinder
FEATURE [Part::Cut] Cut146
  Base = -> Cut145
  Tool = -> Cylinder001
FEATURE [Part::Cut] Cut147
  Base = -> Cut146
  Tool = -> Cylinder002
FEATURE [Part::Cut] Cut148
  Base = -> Cut147
  Tool = -> Cylinder003
FEATURE [Part::Box] Box060  label="Würfel060"
  AttacherType = Attacher::AttachEngine3D
  Height = 7.05
  Length = 162.1
  Placement = pos=(5.95,12.25,5) rot=(0,0,1;0rad)
  Width = 93.8
  expr: .Placement.Base.x = 15.5 - 6.5 - 3 - 0.05
  expr: .Placement.Base.y = 20.8 - 5.5 - 3 - 0.05
  expr: Height = Spreadsheet.B4
FEATURE [Part::Fillet] Fillet027
  Base = -> Box060
  Edges = 4 edges r=2: [Edge1,Edge3,Edge5,Edge7]
FEATURE [Part::Cut] Cut149  label="template"
  Base = -> Cut148
  Tool = -> Fillet027
